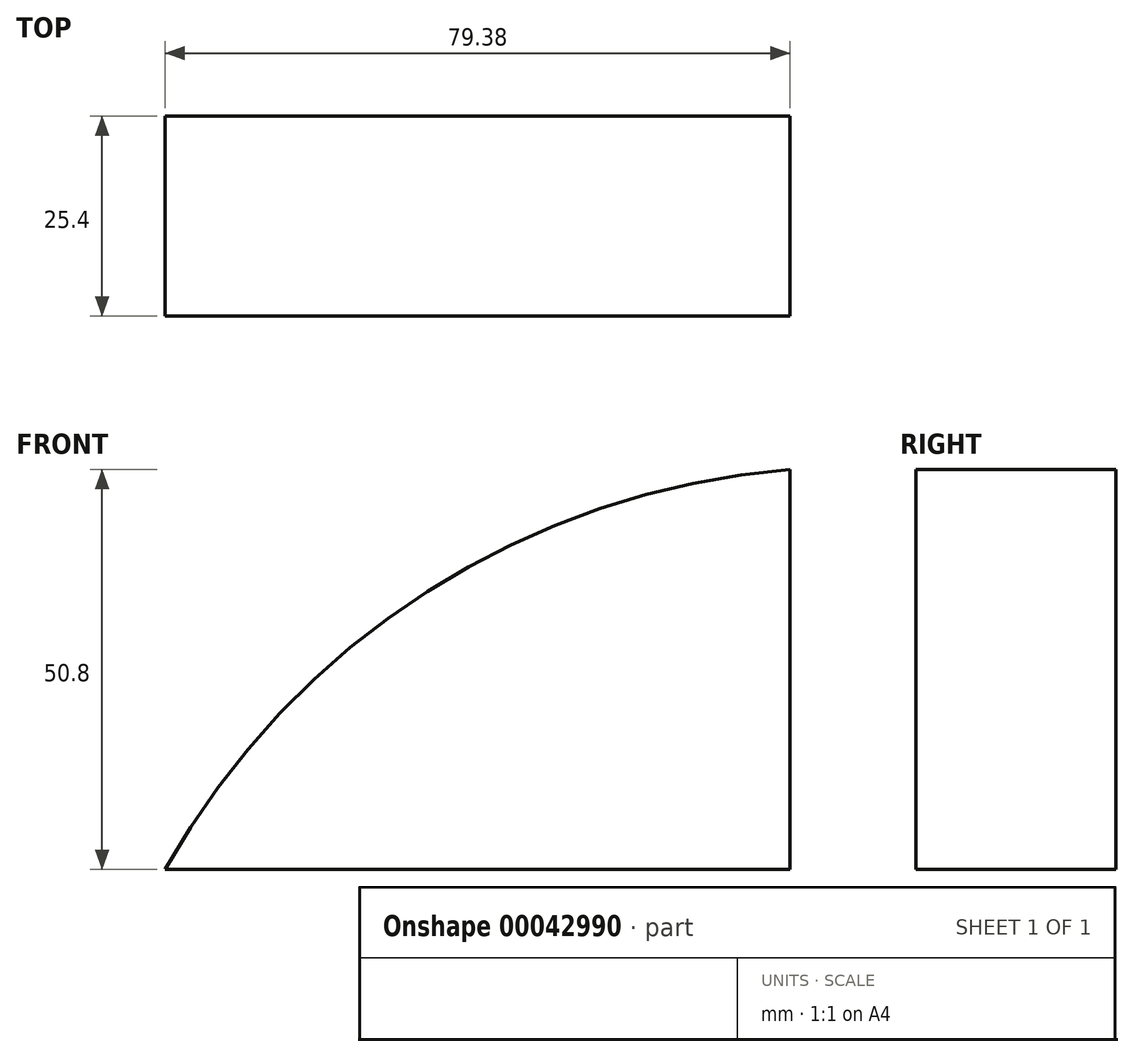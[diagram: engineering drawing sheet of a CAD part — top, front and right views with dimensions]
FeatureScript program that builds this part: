
annotation { "Feature Type Name" : "Feature", "Feature Type Description" : "" }
export const myFeature = defineFeature(function(context is Context, id is Id, definition is map)
    precondition{}
    {
        {
            var Q0;
            Q0=qCreatedBy(makeId("Front.planeOp"),FACE);
            var sketch = newSketch(context, id + "F0", { "sketchPlane" : qUnion([Q0])});
            skLineSegment(sketch, "E0", {"start": v(0, 0) * mm, "end": v(79.38, 0) * mm});
            skLineSegment(sketch, "E1", {"start": v(79.38, 0) * mm, "end": v(79.38, 50.8) * mm});
            skArc(sketch, "E2", {"start": v(79.38, 50.8) * mm, "mid": v(33.33, 35.33) * mm, "end": v(0, 0) * mm});
            skSolve(sketch);
        }
        {
            var Q0;
            Q0=makeQuery(id+"F0.imprint","IMPRINT",FACE,{"disambiguationData":[TD([[makeQuery(id+"F0.imprint","IMPRINT",EDGE,{"derivedFrom":sQuery(id+"F0.wireOp",EDGE,"E0")}),1.0]])]});
            extrude(context, id + "F1", {"entities" : qUnion([Q0]), "depth" : 25.4 * mm});
        }
    });
